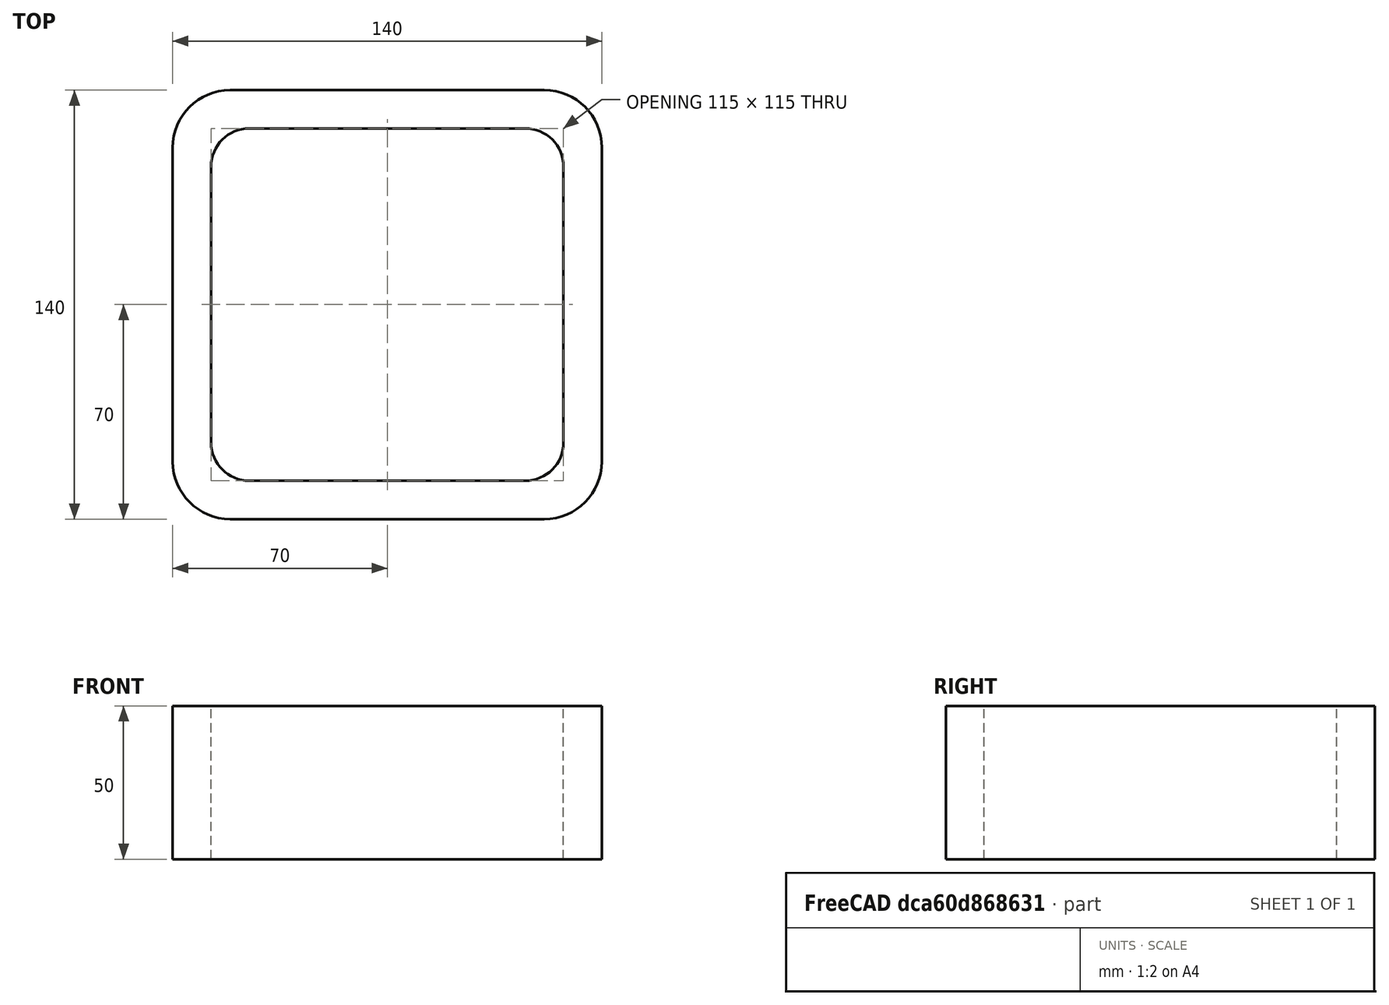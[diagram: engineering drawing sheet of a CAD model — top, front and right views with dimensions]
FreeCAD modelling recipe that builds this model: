
FCSTD DOCUMENT  (FreeCAD 0.15R4671 (Git))
Label: Square hollow section 140x140x12.5 EN10219 S235JRH
License: All rights reserved
LicenseURL: http://en.wikipedia.org/wiki/All_rights_reserved
objects: Sketcher::SketchObject×1, Part::Extrusion×1
note: 2 computed .brp shape members not serialized (recipe doc carries the construction recipe); baked Part::Feature solids carry a one-line shape summary decoded from their .brp

FEATURE [Sketcher::SketchObject] Sketch
  sketch-geometry (16):
    g0: LineSegment StartX=-45 StartY=57.5 StartZ=0 EndX=45 EndY=57.5 EndZ=0
    g1: LineSegment StartX=57.5 StartY=45 StartZ=0 EndX=57.5 EndY=-45 EndZ=0
    g2: LineSegment StartX=45 StartY=-57.5 StartZ=0 EndX=-45 EndY=-57.5 EndZ=0
    g3: LineSegment StartX=-57.5 StartY=-45 StartZ=0 EndX=-57.5 EndY=45 EndZ=0
    g4: LineSegment StartX=-51.25 StartY=70 StartZ=0 EndX=51.25 EndY=70 EndZ=0
    g5: LineSegment StartX=70 StartY=51.25 StartZ=0 EndX=70 EndY=-51.25 EndZ=0
    g6: LineSegment StartX=51.25 StartY=-70 StartZ=0 EndX=-51.25 EndY=-70 EndZ=0
    g7: LineSegment StartX=-70 StartY=-51.25 StartZ=0 EndX=-70 EndY=51.25 EndZ=0
    g8: ArcOfCircle CenterX=-45 CenterY=45 CenterZ=0 NormalX=0 NormalY=0 NormalZ=1 Radius=12.5 StartAngle=1.5708 EndAngle=3.14159
    g9: ArcOfCircle CenterX=45 CenterY=45 CenterZ=0 NormalX=0 NormalY=0 NormalZ=1 Radius=12.5 StartAngle=0 EndAngle=1.5708
    g10: ArcOfCircle CenterX=45 CenterY=-45 CenterZ=0 NormalX=0 NormalY=0 NormalZ=1 Radius=12.5 StartAngle=4.71239 EndAngle=6.28319
    g11: ArcOfCircle CenterX=-45 CenterY=-45 CenterZ=0 NormalX=0 NormalY=0 NormalZ=1 Radius=12.5 StartAngle=3.14159 EndAngle=4.71239
    g12: ArcOfCircle CenterX=51.25 CenterY=51.25 CenterZ=0 NormalX=0 NormalY=0 NormalZ=1 Radius=18.75 StartAngle=0 EndAngle=1.5708
    g13: ArcOfCircle CenterX=51.25 CenterY=-51.25 CenterZ=0 NormalX=0 NormalY=0 NormalZ=1 Radius=18.75 StartAngle=4.71239 EndAngle=6.28319
    g14: ArcOfCircle CenterX=-51.25 CenterY=-51.25 CenterZ=0 NormalX=0 NormalY=0 NormalZ=1 Radius=18.75 StartAngle=3.14159 EndAngle=4.71239
    g15: ArcOfCircle CenterX=-51.25 CenterY=51.25 CenterZ=0 NormalX=0 NormalY=0 NormalZ=1 Radius=18.75 StartAngle=1.5708 EndAngle=3.14159
  constraints (36):
    c: Horizontal(g2)
    c: Vertical(g3)
    c: Horizontal(g6)
    c: Vertical(g7)
    c: Tangent(g3,g8) = 1.5708
    c: Tangent(g0,g8) = 1.5708
    c: Tangent(g0,g9) = 1.5708
    c: Tangent(g1,g9) = 1.5708
    c: Tangent(g1,g10) = 1.5708
    c: Tangent(g2,g10) = 1.5708
    c: Tangent(g2,g11) = 1.5708
    c: Tangent(g3,g11) = 1.5708
    c: Tangent(g4,g12) = 1.5708
    c: Tangent(g5,g12) = 1.5708
    c: Tangent(g5,g13) = 1.5708
    c: Tangent(g6,g13) = 1.5708
    c: Tangent(g6,g14) = 1.5708
    c: Tangent(g7,g14) = 1.5708
    c: Tangent(g7,g15) = 1.5708
    c: Tangent(g4,g15) = 1.5708
    c: Equal(g9,g8)
    c: Equal(g9,g11)
    c: Equal(g9,g10)
    c: Equal(g12,g15)
    c: Equal(g12,g14)
    c: Equal(g12,g13)
    c: Symmetric(g4,g6,g-1)
    c: Symmetric(g7,g5,g-2)
    c: DistanceY(g4,g6) = -140
    c: DistanceX(g7,g5) = 140
    c: Symmetric(g3,g1,g-2)
    c: Symmetric(g0,g2,g-1)
    c: DistanceY(g0,g4) = 12.5
    c: DistanceX(g5,g1) = -12.5
    c: Radius(g9) = 12.5
    c: Radius(g12) = 18.75
FEATURE [Part::Extrusion] Extrude  label="Square hollow section 140x140x12.5 EN10219 S235JRH"
  Base = -> Sketch
  Dir = (0,0,50)
  Solid = true
